# Revit family: SB28
name_source: partatom
category: Modèles génériques
units: mm (PartAtom-declared; Revit-internal decimal feet)

## family parameters
Basée sur le plan de construction = Oui
Cote de connecteur circulaire = Utiliser le diamètre
Couper avec des vides une fois chargée = Non
Numéro OmniClass = 23.85.10.11.14.14.14
Partagée = Non
Peut héberger une armature = Non
Point de calcul de pièce = Non
Titre OmniClass = Loudspeakers
Toujours verticalement = Non
Type d'élément = Normal

## types (1)
- SB28
    Amplified by = LA8 / LA12X
    Cabinet = Baltic birch plywood
    Connectors = IN: 1 x 4 point SpeakON
    Description = SUBWOOFER ENCLOSURE
    Elévation par défaut = 0 mm  [stored 0 ft]
    Fabricant = L-Acoustics
    Finish standard = L-Acoustics - Dark Grey Brown (Pantone 426C)
    Low frequency limit (-10 dB) = 25 Hz ([SB28_100])
    Maximal SPL = 142 dB ([SB28_100])
    Modèle = SB28
    Nominal impedance = 4 Ω
    RMS power handling = 1255 W
    Transducers = LF: 2 x 8''   |   HF: 1 x 3''
    URL = https://www.l-acoustics.com
    Version = v1.0.0

note: [stored X ft] marks values corroborated as IEEE doubles in the binary element streams (Revit-internal decimal feet)
